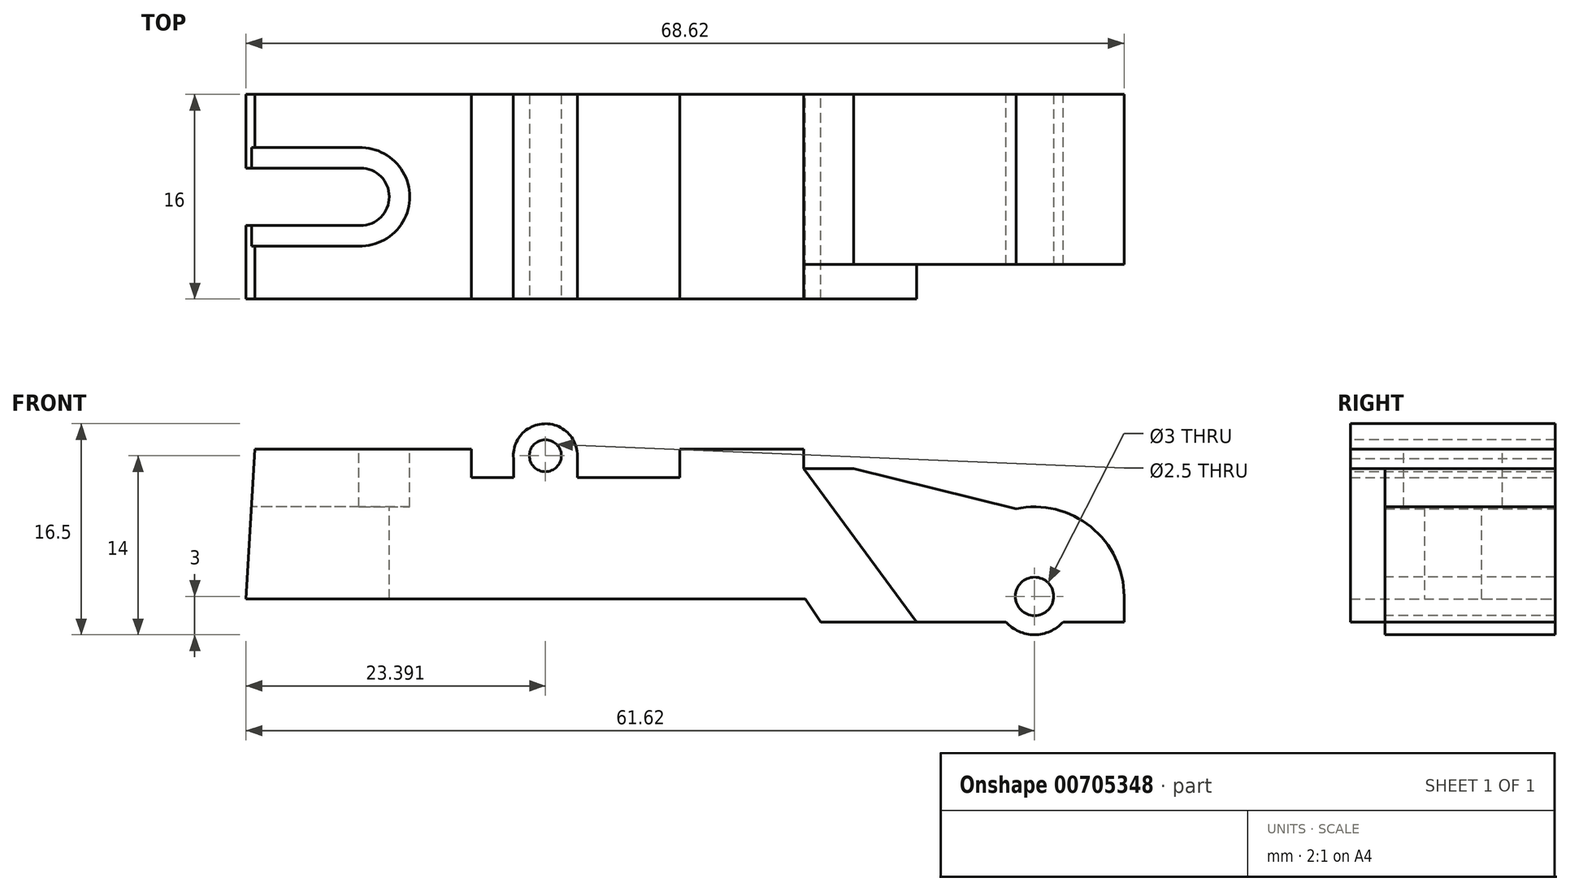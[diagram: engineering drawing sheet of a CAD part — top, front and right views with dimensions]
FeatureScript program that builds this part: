
annotation { "Feature Type Name" : "Feature", "Feature Type Description" : "" }
export const myFeature = defineFeature(function(context is Context, id is Id, definition is map)
    precondition{}
    {
        {
            var Q0;
            Q0=qCreatedBy(makeId("Front.planeOp"),FACE);
            var sketch = newSketch(context, id + "F0", { "sketchPlane" : qUnion([Q0])});
            skLineSegment(sketch, "E0", {"start": v(0, 0) * mm, "end": v(43.7, 0) * mm});
            skLineSegment(sketch, "E1", {"start": v(43.7, 0) * mm, "end": v(44.92, -1.8) * mm});
            skLineSegment(sketch, "E2", {"start": v(44.92, -1.8) * mm, "end": v(59.38, -1.8) * mm});
            skLineSegment(sketch, "E3", {"start": v(68.62, -1.8) * mm, "end": v(68.62, 0.65) * mm});
            skLineSegment(sketch, "E4", {"start": v(47.5, 10.2) * mm, "end": v(43.6, 10.2) * mm});
            skLineSegment(sketch, "E5", {"start": v(43.6, 10.2) * mm, "end": v(43.6, 11.7) * mm});
            skLineSegment(sketch, "E6", {"start": v(43.6, 11.7) * mm, "end": v(33.9, 11.7) * mm});
            skLineSegment(sketch, "E7", {"start": v(33.9, 11.7) * mm, "end": v(33.9, 9.5) * mm});
            skLineSegment(sketch, "E8", {"start": v(33.9, 9.5) * mm, "end": v(25.9, 9.5) * mm});
            skLineSegment(sketch, "E9", {"start": v(25.9, 9.5) * mm, "end": v(25.9, 11.2) * mm});
            skArc(sketch, "E10", {"start": v(25.9, 11.2) * mm, "mid": v(23.28, 13.7) * mm, "end": v(20.9, 10.99) * mm});
            skLineSegment(sketch, "E11", {"start": v(20.9, 10.99) * mm, "end": v(20.9, 9.5) * mm});
            skLineSegment(sketch, "E12", {"start": v(20.9, 9.5) * mm, "end": v(17.6, 9.5) * mm});
            skLineSegment(sketch, "E13", {"start": v(17.6, 9.5) * mm, "end": v(17.6, 11.7) * mm});
            skLineSegment(sketch, "E14", {"start": v(17.6, 11.7) * mm, "end": v(0.7, 11.7) * mm});
            skLineSegment(sketch, "E15", {"start": v(0.7, 11.7) * mm, "end": v(0, 0) * mm});
            skArc(sketch, "E16", {"start": v(68.62, 0.2) * mm, "mid": v(66.03, 5.64) * mm, "end": v(60.18, 7.05) * mm});
            skLineSegment(sketch, "E17", {"start": v(47.5, 10.2) * mm, "end": v(60.18, 7.05) * mm});
            skArc(sketch, "E18", {"start": v(59.38, -1.8) * mm, "mid": v(61.62, -2.8) * mm, "end": v(63.86, -1.8) * mm});
            skLineSegment(sketch, "E19.trimOffspring", {"start": v(63.86, -1.8) * mm, "end": v(68.62, -1.8) * mm});
            skSolve(sketch);
        }
        {
            var Q0;
            Q0 = qSketchRegion(id + "F0", true);
            extrude(context, id + "F1", {"entities" : qUnion([Q0]), "depth" : 16 * mm, "offsetDistance" : 25 * mm});
        }
        {
            var Q0;
            Q0=makeQuery(id+"F1.opExtrude","CAP_FACE",FACE,{"disambiguationData":[OSD([sQuery(id+"F0.wireOp",EDGE,"E0"),sQuery(id+"F0.wireOp",EDGE,"E1"),sQuery(id+"F0.wireOp",EDGE,"E2"),sQuery(id+"F0.wireOp",EDGE,"E3"),sQuery(id+"F0.wireOp",EDGE,"E4"),sQuery(id+"F0.wireOp",EDGE,"E5"),sQuery(id+"F0.wireOp",EDGE,"E6"),sQuery(id+"F0.wireOp",EDGE,"E7"),sQuery(id+"F0.wireOp",EDGE,"E8"),sQuery(id+"F0.wireOp",EDGE,"E9"),sQuery(id+"F0.wireOp",EDGE,"E10"),sQuery(id+"F0.wireOp",EDGE,"E11"),sQuery(id+"F0.wireOp",EDGE,"E12"),sQuery(id+"F0.wireOp",EDGE,"E13"),sQuery(id+"F0.wireOp",EDGE,"E14"),sQuery(id+"F0.wireOp",EDGE,"E15"),sQuery(id+"F0.wireOp",EDGE,"E16"),sQuery(id+"F0.wireOp",EDGE,"E17"),sQuery(id+"F0.wireOp",EDGE,"E18"),sQuery(id+"F0.wireOp",EDGE,"E19.trimOffspring")])],"isStart":false});
            var sketch = newSketch(context, id + "F2", { "sketchPlane" : qUnion([Q0])});
            skCircle(sketch, "E20", {"center": v(23.4, 11.2) * mm, "radius": 1.25 * mm});
            skCircle(sketch, "E21", {"center": v(61.62, 0.2) * mm, "radius": 1.5 * mm});
            skSolve(sketch);
        }
        {
            var Q0;
            Q0=makeQuery(id+"F2.imprint","IMPRINT",FACE,{"disambiguationData":[TD([[makeQuery(id+"F2.imprint","IMPRINT",EDGE,{"derivedFrom":sQuery(id+"F2.wireOp",EDGE,"E21")}),1.0]])]});
            var Q1;
            Q1=makeQuery(id+"F2.imprint","IMPRINT",FACE,{"disambiguationData":[TD([[makeQuery(id+"F2.imprint","IMPRINT",EDGE,{"derivedFrom":sQuery(id+"F2.wireOp",EDGE,"E20")}),1.0]])]});
            extrude(context, id + "F3", {"entities" : qUnion([Q0, Q1]), "operationType" : NewBodyOperationType.REMOVE, "endBound" : BoundingType.THROUGH_ALL, "oppositeDirection" : true, "depth" : 25 * mm, "offsetDistance" : 25 * mm});
        }
        {
            var Q0;
            Q0=makeQuery(id+"F1.opExtrude","CAP_FACE",FACE,{"disambiguationData":[OSD([sQuery(id+"F0.wireOp",EDGE,"E0"),sQuery(id+"F0.wireOp",EDGE,"E1"),sQuery(id+"F0.wireOp",EDGE,"E2"),sQuery(id+"F0.wireOp",EDGE,"E3"),sQuery(id+"F0.wireOp",EDGE,"E4"),sQuery(id+"F0.wireOp",EDGE,"E5"),sQuery(id+"F0.wireOp",EDGE,"E6"),sQuery(id+"F0.wireOp",EDGE,"E7"),sQuery(id+"F0.wireOp",EDGE,"E8"),sQuery(id+"F0.wireOp",EDGE,"E9"),sQuery(id+"F0.wireOp",EDGE,"E10"),sQuery(id+"F0.wireOp",EDGE,"E11"),sQuery(id+"F0.wireOp",EDGE,"E12"),sQuery(id+"F0.wireOp",EDGE,"E13"),sQuery(id+"F0.wireOp",EDGE,"E14"),sQuery(id+"F0.wireOp",EDGE,"E15"),sQuery(id+"F0.wireOp",EDGE,"E16"),sQuery(id+"F0.wireOp",EDGE,"E17"),sQuery(id+"F0.wireOp",EDGE,"E18"),sQuery(id+"F0.wireOp",EDGE,"E19.trimOffspring")])],"isStart":false});
            var sketch = newSketch(context, id + "F4", { "sketchPlane" : qUnion([Q0])});
            skLineSegment(sketch, "E22", {"start": v(43.6, 10.2) * mm, "end": v(52.42, -1.8) * mm});
            skLineSegment(sketch, "E23", {"start": v(43.6, 10.2) * mm, "end": v(69.06, 10.2) * mm});
            skLineSegment(sketch, "E24", {"start": v(69.06, 10.2) * mm, "end": v(70.33, -4.38) * mm});
            skLineSegment(sketch, "E25", {"start": v(70.33, -4.38) * mm, "end": v(58.71, -4.38) * mm});
            skLineSegment(sketch, "E26", {"start": v(58.71, -4.38) * mm, "end": v(52.42, -1.8) * mm});
            skSolve(sketch);
        }
        {
            var Q0;
            Q0 = qSketchRegion(id + "F4", true);
            extrude(context, id + "F5", {"entities" : qUnion([Q0]), "operationType" : NewBodyOperationType.REMOVE, "oppositeDirection" : true, "depth" : 2.7 * mm, "offsetDistance" : 25 * mm});
        }
        {
            var Q0;
            Q0=qCreatedBy(makeId("Front.planeOp"),FACE);
            cPlane(context, id + "F6", {"entities" : qUnion([Q0]), "cplaneType" : CPlaneType.OFFSET, "offset" : 8 * mm, "width" : 150 * mm, "height" : 150 * mm});
        }
        {
            var Q0;
            Q0=makeQuery(id+"F1.opExtrude","SWEPT_FACE",FACE,{"disambiguationData":[OSD([sQuery(id+"F0.wireOp",EDGE,"E14")])]});
            var sketch = newSketch(context, id + "F7", { "sketchPlane" : qUnion([Q0])});
            skLineSegment(sketch, "E27", {"start": v(0.7, -5.75) * mm, "end": v(8.94, -5.75) * mm});
            skLineSegment(sketch, "E28", {"start": v(0.7, -8) * mm, "end": v(68.7, -8) * mm, "construction": true});
            skPoint(sketch, "E29.third.point", {"position": v(6.72, -12.54) * mm});
            skLineSegment(sketch, "E30", {"start": v(8.94, -10.25) * mm, "end": v(0.7, -10.25) * mm});
            skArc(sketch, "E31", {"start": v(8.94, -10.25) * mm, "mid": v(11.2, -8) * mm, "end": v(8.94, -5.75) * mm});
            skPoint(sketch, "E32.orphan", {"position": v(8.91, -5.75) * mm});
            skLineSegment(sketch, "E33", {"start": v(0.7, -5.75) * mm, "end": v(-0.9, -5.75) * mm});
            skLineSegment(sketch, "E34", {"start": v(-0.9, -5.75) * mm, "end": v(-0.9, -10.25) * mm});
            skLineSegment(sketch, "E35", {"start": v(-0.9, -10.25) * mm, "end": v(0.7, -10.25) * mm});
            skSolve(sketch);
        }
        {
            var Q0;
            {var subQ0=sQuery(id+"F7.wireOp",EDGE,"E27");Q0=makeQuery(id+"F7.imprint","IMPRINT",FACE,{"disambiguationData":[TD([[makeQuery(id+"F7.imprint","IMPRINT",EDGE,{"derivedFrom":subQ0}),-1.0]])]});}
            extrude(context, id + "F8", {"entities" : qUnion([Q0]), "operationType" : NewBodyOperationType.REMOVE, "endBound" : BoundingType.THROUGH_ALL, "oppositeDirection" : true, "depth" : 25 * mm, "offsetDistance" : 25 * mm});
        }
        {
            var Q0;
            Q0 = qSketchRegion(id + "F7", true);
            extrude(context, id + "F9", {"entities" : qUnion([Q0]), "operationType" : NewBodyOperationType.REMOVE, "oppositeDirection" : true, "depth" : 25 * mm, "offsetDistance" : 25 * mm});
        }
        {
            var Q0;
            Q0=makeQuery(id+"F1.opExtrude","SWEPT_FACE",FACE,{"disambiguationData":[OSD([sQuery(id+"F0.wireOp",EDGE,"E14")])]});
            var sketch = newSketch(context, id + "F10", { "sketchPlane" : qUnion([Q0])});
            skCircle(sketch, "E36", {"center": v(8.94, -8) * mm, "radius": 3.85 * mm});
            skLineSegment(sketch, "E37", {"start": v(9.06, -4.15) * mm, "end": v(-1.52, -4.15) * mm});
            skLineSegment(sketch, "E38", {"start": v(9.06, -11.85) * mm, "end": v(-2.62, -11.85) * mm});
            skLineSegment(sketch, "E39", {"start": v(-2.62, -11.85) * mm, "end": v(-1.52, -4.15) * mm});
            skSolve(sketch);
        }
        {
            var Q0;
            Q0 = qSketchRegion(id + "F10", true);
            extrude(context, id + "F11", {"entities" : qUnion([Q0]), "operationType" : NewBodyOperationType.REMOVE, "oppositeDirection" : true, "depth" : 4.5 * mm, "offsetDistance" : 25 * mm});
        }
    });
